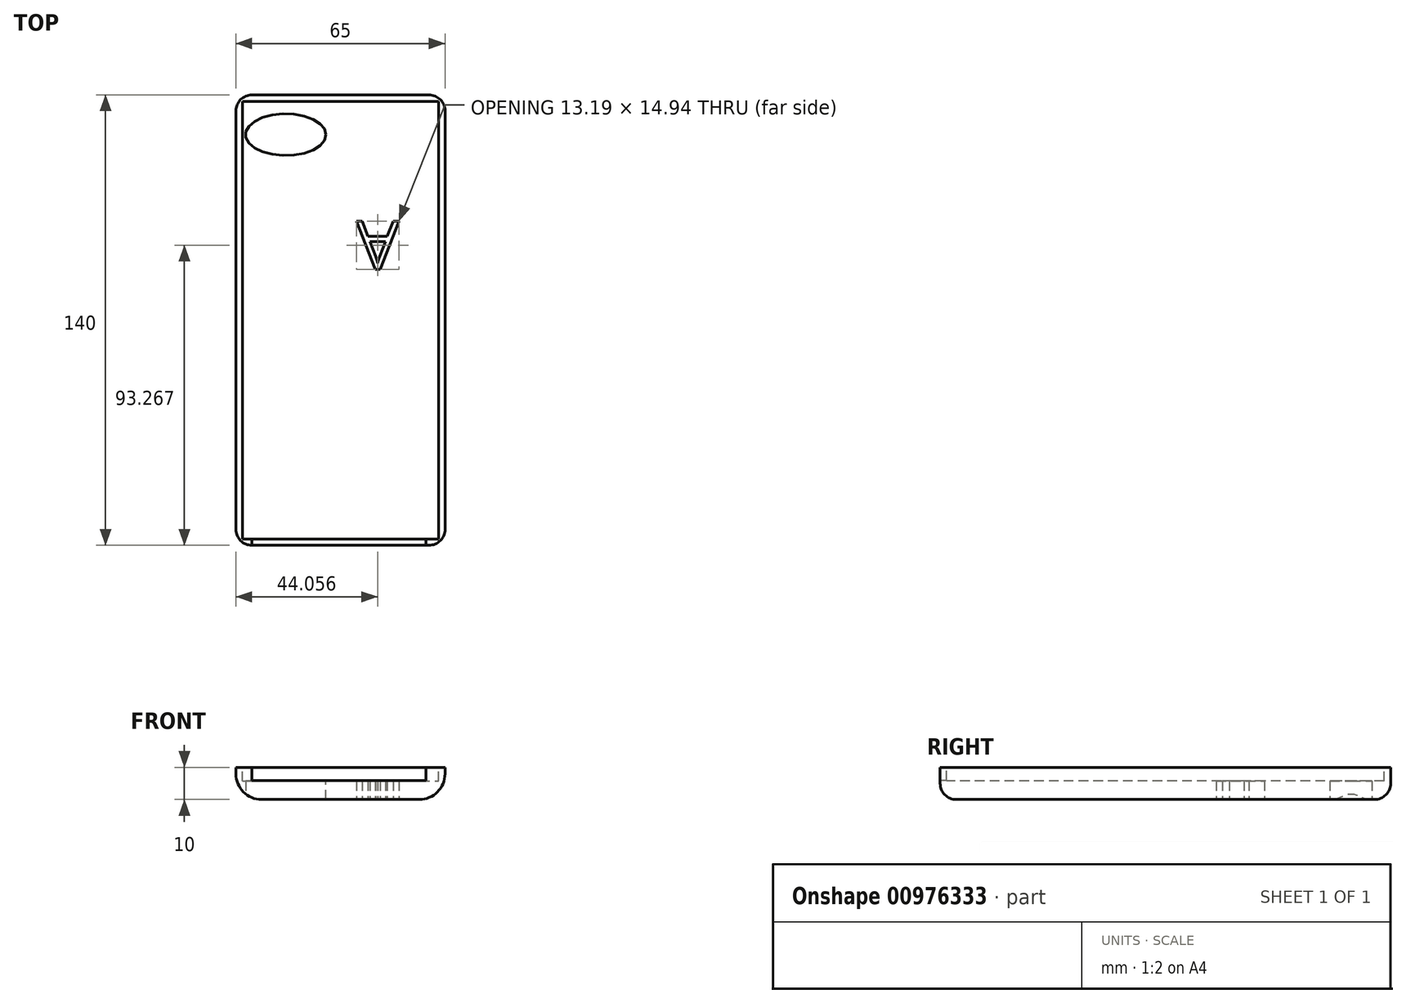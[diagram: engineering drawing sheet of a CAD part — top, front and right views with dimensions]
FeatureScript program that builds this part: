
annotation { "Feature Type Name" : "Feature", "Feature Type Description" : "" }
export const myFeature = defineFeature(function(context is Context, id is Id, definition is map)
    precondition{}
    {
        {
            var Q0;
            Q0=qCreatedBy(makeId("Top.planeOp"),FACE);
            var sketch = newSketch(context, id + "F0", { "sketchPlane" : qUnion([Q0])});
            skLineSegment(sketch, "E0.bottom", {"start": v(-32.5, 70) * mm, "end": v(32.5, 70) * mm});
            skLineSegment(sketch, "E0.top", {"start": v(-32.5, -70) * mm, "end": v(32.5, -70) * mm});
            skLineSegment(sketch, "E0.left", {"start": v(-32.5, 70) * mm, "end": v(-32.5, -70) * mm});
            skLineSegment(sketch, "E0.right", {"start": v(32.5, 70) * mm, "end": v(32.5, -70) * mm});
            skSolve(sketch);
        }
        {
            var Q0;
            Q0 = qSketchRegion(id + "F0", true);
            extrude(context, id + "F1", {"entities" : qUnion([Q0]), "depth" : 10 * mm, "offsetDistance" : 25 * mm});
        }
        {
            var Q0;
            Q0=makeQuery(id+"F1.opExtrude","CAP_EDGE",EDGE,{"disambiguationData":[OSD([sQuery(id+"F0.wireOp",EDGE,"E0.right")])],"isStart":true});
            var Q1;
            Q1=makeQuery(id+"F1.opExtrude","CAP_EDGE",EDGE,{"disambiguationData":[OSD([sQuery(id+"F0.wireOp",EDGE,"E0.left")])],"isStart":true});
            fillet(context, id + "F2", {"entities" : qUnion([Q0, Q1]), "radius" : 8 * mm, "tangentPropagation" : true, "allowEdgeOverflow" : false});
        }
        {
            var Q0;
            Q0=makeQuery(id+"F1.opExtrude","CAP_FACE",FACE,{"disambiguationData":[OSD([sQuery(id+"F0.wireOp",EDGE,"E0.bottom"),sQuery(id+"F0.wireOp",EDGE,"E0.top"),sQuery(id+"F0.wireOp",EDGE,"E0.left"),sQuery(id+"F0.wireOp",EDGE,"E0.right")])],"isStart":false});
            var sketch = newSketch(context, id + "F3", { "sketchPlane" : qUnion([Q0])});
            skLineSegment(sketch, "E1.0", {"start": v(-30.5, 68) * mm, "end": v(-30.5, -68) * mm});
            skLineSegment(sketch, "E1.1", {"start": v(-30.5, 68) * mm, "end": v(30.5, 68) * mm});
            skLineSegment(sketch, "E1.2", {"start": v(30.5, 68) * mm, "end": v(30.5, -68) * mm});
            skLineSegment(sketch, "E1.3", {"start": v(-30.5, -68) * mm, "end": v(30.5, -68) * mm});
            skSolve(sketch);
        }
        {
            var Q0;
            Q0=makeQuery(id+"F3.imprint","IMPRINT",FACE,{"disambiguationData":[TD([[makeQuery(id+"F3.imprint","IMPRINT",EDGE,{"derivedFrom":sQuery(id+"F3.wireOp",EDGE,"E1.0")}),1.0]])]});
            extrude(context, id + "F4", {"entities" : qUnion([Q0]), "operationType" : NewBodyOperationType.ADD, "oppositeDirection" : true, "depth" : 6.5 * mm, "offsetDistance" : 25 * mm});
        }
        {
            var Q0;
            Q0 = qSketchRegion(id + "F3", true);
            extrude(context, id + "F5", {"entities" : qUnion([Q0]), "operationType" : NewBodyOperationType.REMOVE, "oppositeDirection" : true, "depth" : 4.3 * mm, "offsetDistance" : 25 * mm});
        }
        {
            var Q0;
            Q0=makeQuery(id+"F3.imprint","IMPRINT",FACE,{"disambiguationData":[TD([[makeQuery(id+"F3.imprint","IMPRINT",EDGE,{"derivedFrom":sQuery(id+"F3.wireOp",EDGE,"E1.0")}),1.0]])]});
            var sketch = newSketch(context, id + "F6", { "sketchPlane" : qUnion([Q0])});
            skEllipse(sketch, "E2", {"center": v(-17, 57.65) * mm, "majorRadius": 12.5 * mm, "minorRadius": 6.5 * mm, "majorAxis": v(1, 0)});
            skSolve(sketch);
        }
        {
            var Q0;
            Q0=makeQuery(id+"F6.imprint","IMPRINT",FACE,{"disambiguationData":[TD([[makeQuery(id+"F6.imprint","IMPRINT",EDGE,{"derivedFrom":sQuery(id+"F6.wireOp",EDGE,"E2")}),1.0]])]});
            extrude(context, id + "F7", {"entities" : qUnion([Q0]), "operationType" : NewBodyOperationType.REMOVE, "endBound" : BoundingType.THROUGH_ALL, "oppositeDirection" : true, "depth" : 25 * mm, "offsetDistance" : 25 * mm});
        }
        {
            var Q0;
            Q0=makeQuery(id+"F1.opExtrude","CAP_EDGE",EDGE,{"disambiguationData":[OSD([sQuery(id+"F0.wireOp",EDGE,"E0.bottom")])],"isStart":true});
            var Q1;
            Q1=makeQuery(id+"F1.opExtrude","CAP_EDGE",EDGE,{"disambiguationData":[OSD([sQuery(id+"F0.wireOp",EDGE,"E0.top")])],"isStart":true});
            fillet(context, id + "F8", {"entities" : qUnion([Q0, Q1]), "radius" : 5 * mm, "tangentPropagation" : true, "allowEdgeOverflow" : false});
        }
        {
            var Q0;
            Q0=makeQuery(id+"F1.opExtrude","SWEPT_FACE",FACE,{"disambiguationData":[OSD([sQuery(id+"F0.wireOp",EDGE,"E0.top")])]});
            var sketch = newSketch(context, id + "F9", { "sketchPlane" : qUnion([Q0])});
            skLineSegment(sketch, "E3.bottom", {"start": v(-27.5, 10) * mm, "end": v(26.62, 10) * mm});
            skLineSegment(sketch, "E3.top", {"start": v(-27.5, 5.88) * mm, "end": v(26.62, 5.88) * mm});
            skLineSegment(sketch, "E3.left", {"start": v(-27.5, 10) * mm, "end": v(-27.5, 5.88) * mm});
            skLineSegment(sketch, "E3.right", {"start": v(26.62, 10) * mm, "end": v(26.62, 5.88) * mm});
            skSolve(sketch);
        }
        {
            var Q0;
            Q0 = qSketchRegion(id + "F9", true);
            extrude(context, id + "F10", {"entities" : qUnion([Q0]), "operationType" : NewBodyOperationType.REMOVE, "endBound" : BoundingType.UP_TO_NEXT, "oppositeDirection" : true, "depth" : 25 * mm, "offsetDistance" : 25 * mm});
        }
        {
            var Q0;
            Q0=makeQuery(id+"F1.opExtrude","CAP_FACE",FACE,{"disambiguationData":[OSD([sQuery(id+"F0.wireOp",EDGE,"E0.bottom"),sQuery(id+"F0.wireOp",EDGE,"E0.top"),sQuery(id+"F0.wireOp",EDGE,"E0.left"),sQuery(id+"F0.wireOp",EDGE,"E0.right")])],"isStart":true});
            var sketch = newSketch(context, id + "F11", { "sketchPlane" : qUnion([Q0])});
            skText(sketch, "E4", { "text": "A", "fontName": "OpenSans-Regular.ttf"});
            const initialGuessF11  = {"E4": [0.00496, -0.03074, 1, 0, 0.01501]};
            skSetInitialGuess(sketch, initialGuessF11);
            skSolve(sketch);
        }
        {
            var Q0;
            Q0 = qSketchRegion(id + "F11", true);
            extrude(context, id + "F12", {"entities" : qUnion([Q0]), "operationType" : NewBodyOperationType.REMOVE, "endBound" : BoundingType.UP_TO_NEXT, "oppositeDirection" : true, "depth" : 20.1 * mm, "offsetDistance" : 25 * mm});
        }
    });
